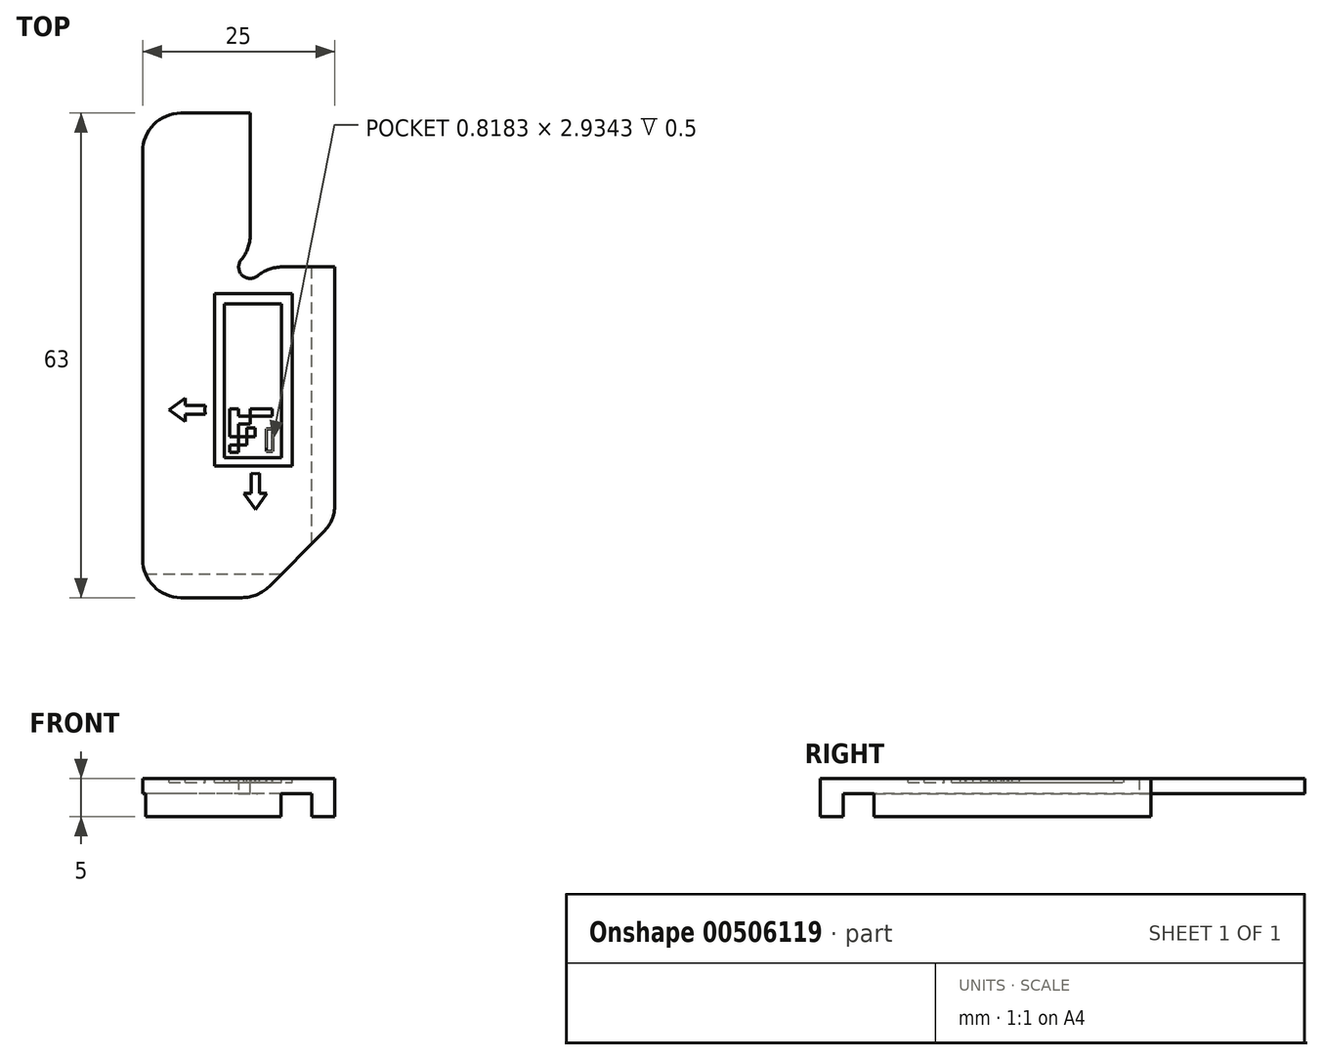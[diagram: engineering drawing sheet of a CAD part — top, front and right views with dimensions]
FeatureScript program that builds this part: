
annotation { "Feature Type Name" : "Feature", "Feature Type Description" : "" }
export const myFeature = defineFeature(function(context is Context, id is Id, definition is map)
    precondition{}
    {
        {
            var Q0;
            Q0=qCreatedBy(makeId("Top.planeOp"),FACE);
            var sketch = newSketch(context, id + "F0", { "sketchPlane" : qUnion([Q0])});
            skLineSegment(sketch, "E0", {"start": v(0, 0) * mm, "end": v(15, 0) * mm});
            skLineSegment(sketch, "E1", {"start": v(15, 0) * mm, "end": v(25, 10) * mm});
            skLineSegment(sketch, "E2", {"start": v(25, 10) * mm, "end": v(25, 43) * mm});
            skLineSegment(sketch, "E3", {"start": v(25, 43) * mm, "end": v(15.5, 43) * mm});
            skLineSegment(sketch, "E4", {"start": v(14, 44.5) * mm, "end": v(14, 63) * mm});
            skLineSegment(sketch, "E5", {"start": v(14, 63) * mm, "end": v(0, 63) * mm});
            skLineSegment(sketch, "E6", {"start": v(0, 63) * mm, "end": v(0, 0) * mm});
            skArc(sketch, "E7", {"start": v(14, 44.5) * mm, "mid": v(12.94, 41.94) * mm, "end": v(15.5, 43) * mm});
            skSolve(sketch);
        }
        {
            var Q0;
            Q0 = qSketchRegion(id + "F0", true);
            extrude(context, id + "F1", {"entities" : qUnion([Q0]), "depth" : 2 * mm});
        }
        {
            var Q0;
            Q0=makeQuery(id+"F1.opExtrude","CAP_FACE",FACE,{"disambiguationData":[OSD([sQuery(id+"F0.wireOp",EDGE,"E0"),sQuery(id+"F0.wireOp",EDGE,"E1"),sQuery(id+"F0.wireOp",EDGE,"E2"),sQuery(id+"F0.wireOp",EDGE,"E3"),sQuery(id+"F0.wireOp",EDGE,"E4"),sQuery(id+"F0.wireOp",EDGE,"E5"),sQuery(id+"F0.wireOp",EDGE,"E6"),sQuery(id+"F0.wireOp",EDGE,"E7")])],"isStart":true});
            var sketch = newSketch(context, id + "F2", { "sketchPlane" : qUnion([Q0])});
            skLineSegment(sketch, "E8", {"start": v(0, 0) * mm, "end": v(15, 0) * mm});
            skLineSegment(sketch, "E9", {"start": v(15, 0) * mm, "end": v(18, -3) * mm});
            skLineSegment(sketch, "E10", {"start": v(18, -3) * mm, "end": v(0, -3) * mm});
            skLineSegment(sketch, "E11", {"start": v(0, -3) * mm, "end": v(0, 0) * mm});
            skLineSegment(sketch, "E12", {"start": v(25, -10) * mm, "end": v(22, -7) * mm});
            skLineSegment(sketch, "E13", {"start": v(22, -7) * mm, "end": v(22, -43) * mm});
            skLineSegment(sketch, "E14", {"start": v(22, -43) * mm, "end": v(25, -43) * mm});
            skLineSegment(sketch, "E15", {"start": v(25, -43) * mm, "end": v(25, -10) * mm});
            skSolve(sketch);
        }
        {
            var Q0;
            Q0 = qSketchRegion(id + "F2", true);
            extrude(context, id + "F3", {"entities" : qUnion([Q0]), "operationType" : NewBodyOperationType.ADD, "depth" : 3 * mm});
        }
        {
            var Q0;
            Q0=makeQuery(id+"F1.opExtrude","SWEPT_EDGE",EDGE,{"disambiguationData":[OSD([sQuery(id+"F0.wireOp",EDGE,"E4"),sQuery(id+"F0.wireOp",EDGE,"E7")])]});
            var Q1;
            Q1=makeQuery(id+"F1.opExtrude","SWEPT_EDGE",EDGE,{"disambiguationData":[OSD([sQuery(id+"F0.wireOp",EDGE,"E3"),sQuery(id+"F0.wireOp",EDGE,"E7")])]});
            fillet(context, id + "F4", {"entities" : qUnion([Q0, Q1]), "radius" : 5 * mm, "tangentPropagation" : true, "allowEdgeOverflow" : false});
        }
        {
            var Q0;
            Q0=makeQuery(id+"F1.opExtrude","SWEPT_EDGE",EDGE,{"disambiguationData":[OSD([sQuery(id+"F0.wireOp",EDGE,"E5"),sQuery(id+"F0.wireOp",EDGE,"E6")])]});
            var Q1;
            Q1=makeQuery(id+"F3.boolean.opBoolean","MERGE",EDGE,{"derivedFrom":[makeQuery(id+"F1.opExtrude","SWEPT_EDGE",EDGE,{"disambiguationData":[OSD([sQuery(id+"F0.wireOp",EDGE,"E0"),sQuery(id+"F0.wireOp",EDGE,"E6")])]}),makeQuery(id+"F3.opExtrude","SWEPT_EDGE",EDGE,{"disambiguationData":[OSD([sQuery(id+"F2.wireOp",EDGE,"E8"),sQuery(id+"F2.wireOp",EDGE,"E11")])]})]});
            var Q2;
            Q2=makeQuery(id+"F3.boolean.opBoolean","MERGE",EDGE,{"derivedFrom":[makeQuery(id+"F1.opExtrude","SWEPT_EDGE",EDGE,{"disambiguationData":[OSD([sQuery(id+"F0.wireOp",EDGE,"E0"),sQuery(id+"F0.wireOp",EDGE,"E1")])]}),makeQuery(id+"F3.opExtrude","SWEPT_EDGE",EDGE,{"disambiguationData":[OSD([sQuery(id+"F2.wireOp",EDGE,"E8"),sQuery(id+"F2.wireOp",EDGE,"E9")])]})]});
            var Q3;
            Q3=makeQuery(id+"F3.boolean.opBoolean","MERGE",EDGE,{"derivedFrom":[makeQuery(id+"F1.opExtrude","SWEPT_EDGE",EDGE,{"disambiguationData":[OSD([sQuery(id+"F0.wireOp",EDGE,"E1"),sQuery(id+"F0.wireOp",EDGE,"E2")])]}),makeQuery(id+"F3.opExtrude","SWEPT_EDGE",EDGE,{"disambiguationData":[OSD([sQuery(id+"F2.wireOp",EDGE,"E12"),sQuery(id+"F2.wireOp",EDGE,"E15")])]})]});
            fillet(context, id + "F5", {"entities" : qUnion([Q0, Q1, Q2, Q3]), "radius" : 5 * mm, "tangentPropagation" : true, "allowEdgeOverflow" : false});
        }
        {
            var Q0;
            Q0=makeQuery(id+"F1.opExtrude","CAP_FACE",FACE,{"disambiguationData":[OSD([sQuery(id+"F0.wireOp",EDGE,"E0"),sQuery(id+"F0.wireOp",EDGE,"E1"),sQuery(id+"F0.wireOp",EDGE,"E2"),sQuery(id+"F0.wireOp",EDGE,"E3"),sQuery(id+"F0.wireOp",EDGE,"E4"),sQuery(id+"F0.wireOp",EDGE,"E5"),sQuery(id+"F0.wireOp",EDGE,"E6"),sQuery(id+"F0.wireOp",EDGE,"E7")])],"isStart":false});
            var sketch = newSketch(context, id + "F6", { "sketchPlane" : qUnion([Q0])});
            skLineSegment(sketch, "E16.bottom", {"start": v(9.36, 17.1) * mm, "end": v(19.47, 17.1) * mm});
            skLineSegment(sketch, "E16.top", {"start": v(9.36, 39.5) * mm, "end": v(19.47, 39.5) * mm});
            skLineSegment(sketch, "E16.left", {"start": v(9.36, 17.1) * mm, "end": v(9.36, 39.5) * mm});
            skLineSegment(sketch, "E16.right", {"start": v(19.47, 17.1) * mm, "end": v(19.47, 39.5) * mm});
            skLineSegment(sketch, "E17.bottom", {"start": v(10.63, 18.22) * mm, "end": v(18.08, 18.22) * mm});
            skLineSegment(sketch, "E17.top", {"start": v(10.63, 38.2) * mm, "end": v(18.08, 38.2) * mm});
            skLineSegment(sketch, "E17.left", {"start": v(10.63, 18.22) * mm, "end": v(10.63, 38.2) * mm});
            skLineSegment(sketch, "E17.right", {"start": v(18.08, 18.22) * mm, "end": v(18.08, 38.2) * mm});
            skLineSegment(sketch, "E18.bottom", {"start": v(11.33, 18.88) * mm, "end": v(12.44, 18.88) * mm});
            skLineSegment(sketch, "E18.top", {"start": v(11.33, 19.87) * mm, "end": v(12.33, 19.87) * mm});
            skLineSegment(sketch, "E18.left", {"start": v(11.33, 18.88) * mm, "end": v(11.33, 19.87) * mm});
            skLineSegment(sketch, "E18.right", {"start": v(12.44, 18.88) * mm, "end": v(12.44, 19.76) * mm});
            skLineSegment(sketch, "E19.bottom", {"start": v(12.56, 19.87) * mm, "end": v(13.56, 19.87) * mm});
            skLineSegment(sketch, "E19.top", {"start": v(12.56, 20.9) * mm, "end": v(13.44, 20.9) * mm});
            skLineSegment(sketch, "E19.left", {"start": v(12.44, 19.98) * mm, "end": v(12.44, 20.8) * mm});
            skLineSegment(sketch, "E19.right", {"start": v(13.56, 19.87) * mm, "end": v(13.56, 20.8) * mm});
            skLineSegment(sketch, "E20.bottom", {"start": v(12.33, 20.9) * mm, "end": v(11.33, 20.9) * mm});
            skLineSegment(sketch, "E20.left", {"start": v(11.33, 20.9) * mm, "end": v(11.33, 22.05) * mm});
            skLineSegment(sketch, "E21.bottom", {"start": v(12.44, 22.57) * mm, "end": v(14, 22.57) * mm});
            skLineSegment(sketch, "E21.top", {"start": v(12.44, 23.6) * mm, "end": v(13.89, 23.6) * mm});
            skLineSegment(sketch, "E21.right", {"start": v(14, 22.57) * mm, "end": v(14, 23.49) * mm});
            skLineSegment(sketch, "E22.bottom", {"start": v(11.33, 24.55) * mm, "end": v(12.44, 24.55) * mm});
            skLineSegment(sketch, "E22.left", {"start": v(11.33, 24.55) * mm, "end": v(11.33, 22.05) * mm});
            skLineSegment(sketch, "E22.right", {"start": v(12.44, 24.55) * mm, "end": v(12.44, 23.6) * mm});
            skLineSegment(sketch, "E23.bottom", {"start": v(16.09, 19.04) * mm, "end": v(16.9, 19.04) * mm});
            skLineSegment(sketch, "E23.top", {"start": v(16.09, 21.97) * mm, "end": v(16.9, 21.97) * mm});
            skLineSegment(sketch, "E23.left", {"start": v(16.09, 19.04) * mm, "end": v(16.09, 21.97) * mm});
            skLineSegment(sketch, "E23.right", {"start": v(16.9, 19.04) * mm, "end": v(16.9, 21.97) * mm});
            skLineSegment(sketch, "E24.bottom", {"start": v(13.67, 20.9) * mm, "end": v(14.63, 20.9) * mm});
            skLineSegment(sketch, "E24.top", {"start": v(13.56, 22.1) * mm, "end": v(14.63, 22.1) * mm});
            skLineSegment(sketch, "E24.left", {"start": v(13.56, 21.01) * mm, "end": v(13.56, 22.1) * mm});
            skLineSegment(sketch, "E24.right", {"start": v(14.63, 20.9) * mm, "end": v(14.63, 22.1) * mm});
            skLineSegment(sketch, "E25.bottom", {"start": v(14.11, 23.6) * mm, "end": v(16.85, 23.6) * mm});
            skLineSegment(sketch, "E25.top", {"start": v(14, 24.52) * mm, "end": v(16.85, 24.52) * mm});
            skLineSegment(sketch, "E25.left", {"start": v(14, 23.71) * mm, "end": v(14, 24.52) * mm});
            skLineSegment(sketch, "E25.right", {"start": v(16.85, 23.6) * mm, "end": v(16.85, 24.52) * mm});
            skLineSegment(sketch, "E26", {"start": v(12.44, 21.01) * mm, "end": v(12.44, 22.57) * mm});
            skLineSegment(sketch, "E27", {"start": v(8.1, 24.43) * mm, "end": v(3.44, 24.43) * mm, "construction": true});
            skLineSegment(sketch, "E28", {"start": v(3.44, 24.43) * mm, "end": v(5.57, 22.91) * mm});
            skLineSegment(sketch, "E29", {"start": v(5.57, 22.91) * mm, "end": v(5.57, 23.87) * mm});
            skLineSegment(sketch, "E30", {"start": v(5.57, 23.87) * mm, "end": v(8.15, 23.87) * mm});
            skLineSegment(sketch, "E31", {"start": v(8.15, 23.87) * mm, "end": v(8.1, 24.43) * mm});
            skLineSegment(sketch, "E32.MirrorCS", {"start": v(8.15, 24.99) * mm, "end": v(8.1, 24.43) * mm});
            skLineSegment(sketch, "E33.MirrorCS", {"start": v(5.57, 25.94) * mm, "end": v(5.57, 24.99) * mm});
            skLineSegment(sketch, "E34.MirrorCS", {"start": v(3.44, 24.43) * mm, "end": v(5.57, 25.94) * mm});
            skLineSegment(sketch, "E35.MirrorCS", {"start": v(5.57, 24.99) * mm, "end": v(8.15, 24.99) * mm});
            skLineSegment(sketch, "E36", {"start": v(14.67, 16.1) * mm, "end": v(14.67, 11.44) * mm, "construction": true});
            skLineSegment(sketch, "E37", {"start": v(14.67, 11.44) * mm, "end": v(16.19, 13.58) * mm});
            skLineSegment(sketch, "E38", {"start": v(16.19, 13.58) * mm, "end": v(15.23, 13.58) * mm});
            skLineSegment(sketch, "E39", {"start": v(15.23, 13.58) * mm, "end": v(15.23, 16.15) * mm});
            skLineSegment(sketch, "E40", {"start": v(15.23, 16.15) * mm, "end": v(14.67, 16.1) * mm});
            skLineSegment(sketch, "E41.MirrorCS", {"start": v(14.11, 16.15) * mm, "end": v(14.67, 16.1) * mm});
            skLineSegment(sketch, "E42.MirrorCS", {"start": v(13.16, 13.58) * mm, "end": v(14.11, 13.58) * mm});
            skLineSegment(sketch, "E43.MirrorCS", {"start": v(14.67, 11.44) * mm, "end": v(13.16, 13.58) * mm});
            skLineSegment(sketch, "E44.MirrorCS", {"start": v(14.11, 13.58) * mm, "end": v(14.11, 16.15) * mm});
            skPoint(sketch, "E45.visualSharp", {"position": v(12.44, 19.87) * mm});
            skArc(sketch, "E45.filletArc", {"start": v(12.56, 19.87) * mm, "mid": v(12.48, 19.84) * mm, "end": v(12.44, 19.76) * mm});
            skArc(sketch, "E46.filletArc", {"start": v(12.33, 19.87) * mm, "mid": v(12.41, 19.9) * mm, "end": v(12.44, 19.98) * mm});
            skPoint(sketch, "E47.visualSharp", {"position": v(12.44, 20.9) * mm});
            skArc(sketch, "E47.filletArc", {"start": v(12.44, 21.01) * mm, "mid": v(12.48, 20.94) * mm, "end": v(12.56, 20.9) * mm});
            skArc(sketch, "E48.filletArc", {"start": v(12.44, 20.8) * mm, "mid": v(12.41, 20.87) * mm, "end": v(12.33, 20.9) * mm});
            skPoint(sketch, "E49.visualSharp", {"position": v(13.56, 20.9) * mm});
            skArc(sketch, "E49.filletArc", {"start": v(13.67, 20.9) * mm, "mid": v(13.59, 20.87) * mm, "end": v(13.56, 20.8) * mm});
            skArc(sketch, "E50.filletArc", {"start": v(13.44, 20.9) * mm, "mid": v(13.52, 20.94) * mm, "end": v(13.56, 21.01) * mm});
            skPoint(sketch, "E51.visualSharp", {"position": v(14, 23.6) * mm});
            skArc(sketch, "E51.filletArc", {"start": v(14.11, 23.6) * mm, "mid": v(14.03, 23.57) * mm, "end": v(14, 23.49) * mm});
            skArc(sketch, "E52.filletArc", {"start": v(13.89, 23.6) * mm, "mid": v(13.97, 23.63) * mm, "end": v(14, 23.71) * mm});
            skSolve(sketch);
        }
        {
            var Q0;
            Q0 = qSketchRegion(id + "F6", true);
            var Q1;
            Q1=makeQuery(id+"F6.imprint","IMPRINT",FACE,{"disambiguationData":[TD([[makeQuery(id+"F6.imprint","IMPRINT",EDGE,{"derivedFrom":sQuery(id+"F6.wireOp",EDGE,"E18.bottom")}),1.0]])]});
            var Q2;
            Q2=makeQuery(id+"F6.imprint","IMPRINT",FACE,{"disambiguationData":[TD([[makeQuery(id+"F6.imprint","IMPRINT",EDGE,{"derivedFrom":sQuery(id+"F6.wireOp",EDGE,"E23.bottom")}),1.0]])]});
            extrude(context, id + "F7", {"entities" : qUnion([Q0, Q1, Q2]), "operationType" : NewBodyOperationType.REMOVE, "oppositeDirection" : true, "depth" : 0.5 * mm});
        }
    });
